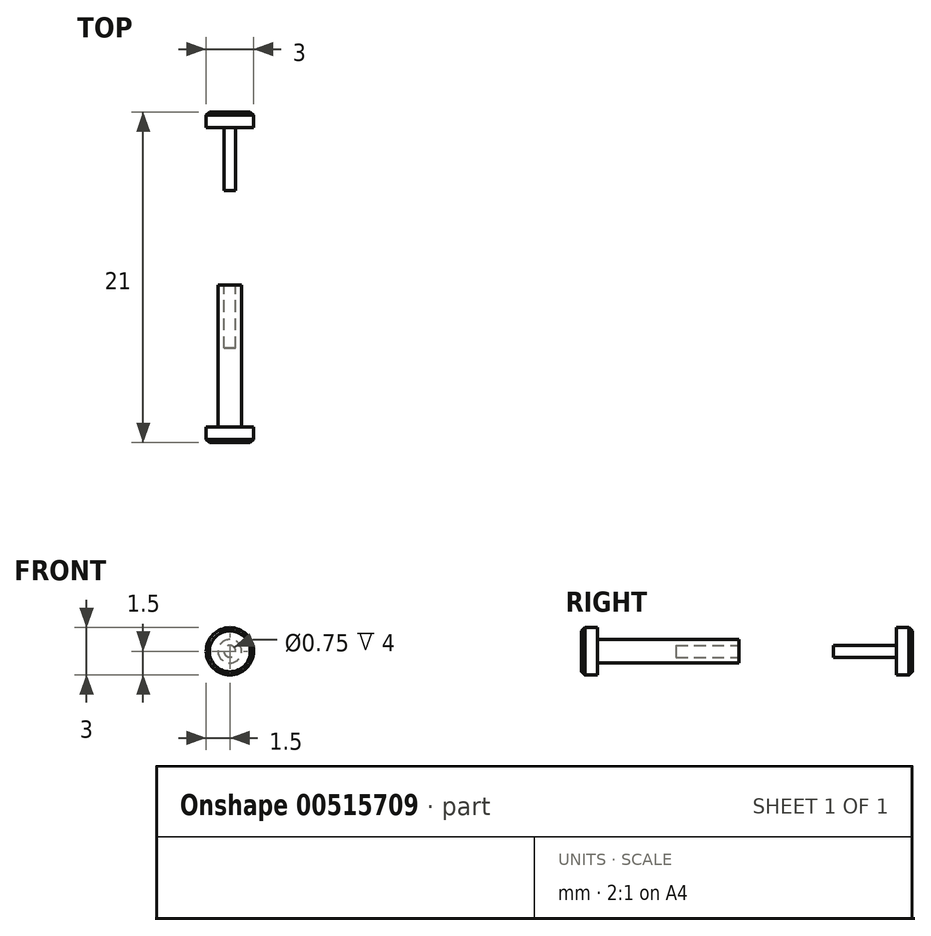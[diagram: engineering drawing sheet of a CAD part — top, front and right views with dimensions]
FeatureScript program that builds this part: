
annotation { "Feature Type Name" : "Feature", "Feature Type Description" : "" }
export const myFeature = defineFeature(function(context is Context, id is Id, definition is map)
    precondition{}
    {
        {
            var Q0;
            Q0=qCreatedBy(makeId("Front.planeOp"),FACE);
            var sketch = newSketch(context, id + "F0", { "sketchPlane" : qUnion([Q0])});
            skCircle(sketch, "E0", {"center": v(0, 0) * mm, "radius": 1.5 * mm});
            skCircle(sketch, "E1", {"center": v(0, 0) * mm, "radius": 0.75 * mm});
            skSolve(sketch);
        }
        {
            var Q0;
            Q0=makeQuery(id+"F0.imprint","IMPRINT",FACE,{"disambiguationData":[TD([[makeQuery(id+"F0.imprint","IMPRINT",EDGE,{"derivedFrom":sQuery(id+"F0.wireOp",EDGE,"E0")}),1.0]])]});
            var Q1;
            Q1=makeQuery(id+"F0.imprint","IMPRINT",FACE,{"disambiguationData":[TD([[makeQuery(id+"F0.imprint","IMPRINT",EDGE,{"derivedFrom":sQuery(id+"F0.wireOp",EDGE,"E1")}),1.0]])]});
            extrude(context, id + "F1", {"entities" : qUnion([Q0, Q1]), "depth" : 1 * mm, "offsetDistance" : 25 * mm});
        }
        {
            var Q0;
            Q0=makeQuery(id+"F0.imprint","IMPRINT",FACE,{"disambiguationData":[TD([[makeQuery(id+"F0.imprint","IMPRINT",EDGE,{"derivedFrom":sQuery(id+"F0.wireOp",EDGE,"E1")}),1.0]])]});
            extrude(context, id + "F2", {"entities" : qUnion([Q0]), "operationType" : NewBodyOperationType.ADD, "oppositeDirection" : true, "depth" : 9 * mm, "offsetDistance" : 25 * mm});
        }
        {
            var Q0;
            Q0=makeQuery(id+"F2.opExtrude","CAP_FACE",FACE,{"disambiguationData":[OSD([sQuery(id+"F0.wireOp",EDGE,"E1")])],"isStart":false});
            var sketch = newSketch(context, id + "F3", { "sketchPlane" : qUnion([Q0])});
            skCircle(sketch, "E2", {"center": v(0, 0) * mm, "radius": 0.38 * mm});
            skSolve(sketch);
        }
        {
            var Q0;
            Q0=makeQuery(id+"F3.imprint","IMPRINT",FACE,{"disambiguationData":[TD([[makeQuery(id+"F3.imprint","IMPRINT",EDGE,{"derivedFrom":sQuery(id+"F3.wireOp",EDGE,"E2")}),1.0]])]});
            extrude(context, id + "F4", {"entities" : qUnion([Q0]), "operationType" : NewBodyOperationType.REMOVE, "oppositeDirection" : true, "depth" : 4 * mm, "offsetDistance" : 25 * mm});
        }
        {
            var Q0;
            Q0=qCreatedBy(makeId("Front.planeOp"),FACE);
            cPlane(context, id + "F5", {"entities" : qUnion([Q0]), "cplaneType" : CPlaneType.OFFSET, "offset" : 20 * mm, "oppositeDirection" : true, "width" : 150 * mm, "height" : 150 * mm});
        }
        {
            var Q0;
            Q0=qCreatedBy(id+"F5.planeOp",FACE);
            var sketch = newSketch(context, id + "F6", { "sketchPlane" : qUnion([Q0])});
            skCircle(sketch, "E3", {"center": v(0, 0) * mm, "radius": 1.5 * mm});
            skCircle(sketch, "E4", {"center": v(0, 0) * mm, "radius": 0.38 * mm});
            skSolve(sketch);
        }
        {
            var Q0;
            Q0=makeQuery(id+"F6.imprint","IMPRINT",FACE,{"disambiguationData":[TD([[makeQuery(id+"F6.imprint","IMPRINT",EDGE,{"derivedFrom":sQuery(id+"F6.wireOp",EDGE,"E3")}),1.0]])]});
            var Q1;
            Q1=makeQuery(id+"F6.imprint","IMPRINT",FACE,{"disambiguationData":[TD([[makeQuery(id+"F6.imprint","IMPRINT",EDGE,{"derivedFrom":sQuery(id+"F6.wireOp",EDGE,"E4")}),1.0]])]});
            extrude(context, id + "F7", {"entities" : qUnion([Q0, Q1]), "depth" : 1 * mm, "offsetDistance" : 25 * mm});
        }
        {
            var Q0;
            Q0=makeQuery(id+"F6.imprint","IMPRINT",FACE,{"disambiguationData":[TD([[makeQuery(id+"F6.imprint","IMPRINT",EDGE,{"derivedFrom":sQuery(id+"F6.wireOp",EDGE,"E4")}),1.0]])]});
            extrude(context, id + "F8", {"entities" : qUnion([Q0]), "operationType" : NewBodyOperationType.ADD, "depth" : 5 * mm, "offsetDistance" : 25 * mm});
        }
        {
            var Q0;
            Q0=makeQuery(id+"F1.opExtrude","CAP_EDGE",EDGE,{"disambiguationData":[OSD([sQuery(id+"F0.wireOp",EDGE,"E0")])],"isStart":false});
            var Q1;
            Q1=makeQuery(id+"F7.opExtrude","CAP_EDGE",EDGE,{"disambiguationData":[OSD([sQuery(id+"F6.wireOp",EDGE,"E3")])],"isStart":true});
            chamfer(context, id + "F9", {"entities" : qUnion([Q0, Q1]), "width" : .2 * mm, "tangentPropagation" : true});
        }
    });
